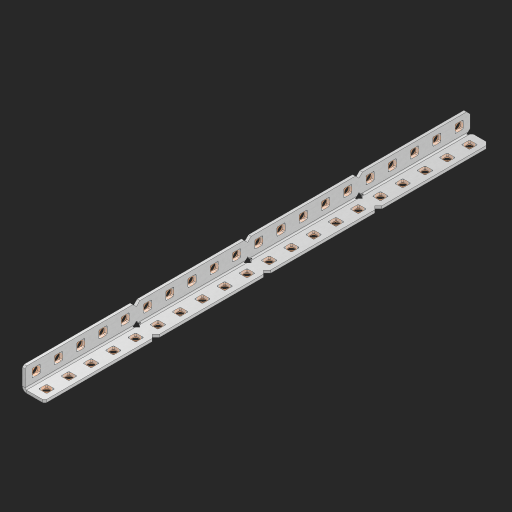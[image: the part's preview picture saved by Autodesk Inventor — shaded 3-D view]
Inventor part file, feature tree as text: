
AUTODESK INVENTOR PART (.ipt)
format: ipt  version: 2023 (Build 270158000, 158)  size: 812,544 bytes
history: native  units: in
note: dims shown in document units (in); Inventor stores cm internally (conversion verified against a paired STEP export)
features: other x46, extrude x41, sheet_metal_op x8, sketch x5, pattern_linear x1, mirror x1, chamfer x1
ambient origin geometry x8: Origin, YZ Plane, XZ Plane, XY Plane, X Axis, Y Axis, Z Axis, Center Point
bodies: Solid1 (feature_tree), Body (feature_tree)
feature tree (103):
  sheet_metal_op  "Flanges"
  sheet_metal_op  "Body Pattern"
  other  "Arc Length"
  pattern_linear  "Notch Pattern"  Spacing1=0.125in  [1 undecoded]
  other  "Diagonal Plane"
  mirror  "Everything Mirrored"
  chamfer  "End Chamfer"
  sketch  "Sketch1"  dims[d0=0.5in]
  other  "Plate1"
  sketch  "Sketch2"  dims[d1=10.0in]
  other  "Plate2"
  sheet_metal_op  "Bend1"
  sheet_metal_op  "Corner1"
  sketch  "Sketch8"  dims[d2=0.0625in]
  sketch  "Sketch9"  dims[d3=0.0625in]
  other  "Srf91"
  sheet_metal_op  "Body Pattern Sketch"
  other  "Srf92"
  sketch  "Sketch13"  dims[d4=0.0312in d5=0.125in d6=0.0625in d7=0.5in d8=90.0deg d9=0.0312in d10=0.25in d11=0.0625in d12=0.0625in d49=0.182in d50=0.02in d52=0.25in d53=0.0625in d54=0.0in d55=0.172in d56=1.0in d57=0.0in d85=0.1473in d86=0.1782in d89=0.0625in d90=0.0in d91=0.04in d92=0.0491in d95=2.5in d96=0.04in d97=0.25in d98=45.0deg d123=0.204in d126=0.0491in d127=0.1473in d128=0.08in d129=0.04in d130=2.5in d131=7.874in d133=0.5in d134=0.3937in d136=1.0in]
  other  "Srf856"
  other  "Srf857"
  other  "Srf858"
  other  "Srf859"
  other  "Srf860"
  other  "Srf861"
  other  "Srf1275"
  other  "Srf1276"
  other  "Srf1278"
  other  "Srf1279"
  other  "Srf1280"
  other  "Srf1281"
  other  "Srf1282"
  other  "Srf1283"
  other  "Srf1383"
  other  "Srf1384"
  other  "Srf1385"
  other  "Srf1386"
  other  "Srf1387"
  other  "Srf1388"
  other  "Srf1389"
  other  "Srf1390"
  other  "Srf1391"
  other  "Srf1392"
  other  "Srf1393"
  other  "Srf1394"
  other  "Srf1395"
  other  "Srf1475"
  other  "Srf1476"
  other  "Srf1477"
  other  "Srf1478"
  other  "Srf1479"
  other  "Srf1480"
  other  "Srf1481"
  other  "Srf1482"
  other  "Srf1483"
  other  "Srf1484"
  other  "Srf1485"
  other  "Srf1486"
  other  "Srf1487"
  sheet_metal_op  "Body Stamp"
  sheet_metal_op  "Body Circle"
  sheet_metal_op  "Notch"
  extrude  "ExtrusionSrf92"  Depth=0.0625in
  extrude  "ExtrusionSrf856"  Depth=0.5in TaperAngle=90.0deg
  extrude  "ExtrusionSrf857"  Depth=0.25in
  extrude  "ExtrusionSrf858"  Depth=0.0625in
  extrude  "ExtrusionSrf859"  Depth=0.0625in
  extrude  "ExtrusionSrf860"  Depth=0.3937in
  extrude  "ExtrusionSrf861"  Depth=0.02in
  extrude  "ExtrusionSrf1275"  Depth=0.25in
  extrude  "ExtrusionSrf1276"  Depth=0.0625in
  extrude  "ExtrusionSrf1277"  TaperAngle=0.0deg  [1 undecoded]
  extrude  "ExtrusionSrf1278"  Depth=0.3937in
  extrude  "ExtrusionSrf1279"  Depth=0.3937in TaperAngle=0.0deg
  extrude  "ExtrusionSrf1280"  Depth=0.3937in
  extrude  "ExtrusionSrf1281"  Depth=0.3937in
  extrude  "ExtrusionSrf1282"  Depth=0.0625in
  extrude  "ExtrusionSrf1383"  Depth=0.3937in TaperAngle=0.0deg
  extrude  "ExtrusionSrf1384"  Depth=0.3937in
  extrude  "ExtrusionSrf1385"  Depth=0.25in TaperAngle=45.0deg
  extrude  "ExtrusionSrf1386"  Depth=0.3937in
  extrude  "ExtrusionSrf1387"  Depth=0.3937in
  extrude  "ExtrusionSrf1388"  Depth=0.3937in
  extrude  "ExtrusionSrf1389"  Depth=0.3937in
  extrude  "ExtrusionSrf1390"  Depth=0.3937in
  extrude  "ExtrusionSrf1391"  Depth=0.3937in
  extrude  "ExtrusionSrf1392"  Depth=0.3937in
  extrude  "ExtrusionSrf1393"  Depth=0.5in
  extrude  "ExtrusionSrf1394"  [1 undecoded]
  extrude  "ExtrusionSrf1395"  [1 undecoded]
  extrude  "ExtrusionSrf1475"  [1 undecoded]
  extrude  "ExtrusionSrf1476"  [1 undecoded]
  extrude  "ExtrusionSrf1477"  [1 undecoded]
  extrude  "ExtrusionSrf1478"  [1 undecoded]
  extrude  "ExtrusionSrf1479"  [1 undecoded]
  extrude  "ExtrusionSrf1480"  [1 undecoded]
  extrude  "ExtrusionSrf1481"  [1 undecoded]
  extrude  "ExtrusionSrf1482"  [1 undecoded]
  extrude  "ExtrusionSrf1483"  [1 undecoded]
  extrude  "ExtrusionSrf1484"  [1 undecoded]
  extrude  "ExtrusionSrf1485"  [1 undecoded]
  extrude  "ExtrusionSrf1486"  [1 undecoded]
  extrude  "ExtrusionSrf1487"  [1 undecoded]
note: 17 required parameter values undecoded (feature->parameter linkage not recoverable at this tier; creation-order binding heuristic only, values carry confidence <= 0.55)
